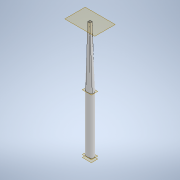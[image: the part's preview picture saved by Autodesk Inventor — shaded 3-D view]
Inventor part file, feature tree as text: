
AUTODESK INVENTOR PART (.ipt)
format: ipt  version: 2021 (Build 250183000, 183)  size: 248,320 bytes
history: native  units: mm
features: sketch x7, loft x6, other x4, plane x3
ambient origin geometry x8: Origin, YZ Plane, XZ Plane, XY Plane, X Axis, Y Axis, Z Axis, Center Point
bodies: Body1 (feature_tree)
feature tree (20):
  sketch  "Sketch1"  dims[d0=463.0mm d8=22.0mm]
  plane  "Work Plane1"
  sketch  "Sketch2"  dims[d9=32.0mm d11=19.0mm]
  sketch  "Sketch3"  dims[d16=15.0mm d17=15.0mm]
  plane  "Work Plane3"
  sketch  "Sketch5"  dims[d19=20.0mm d20=30.0mm]
  sketch  "Sketch6"  dims[d25=-455.0mm d26=20.0mm d27=22.0mm]
  sketch  "Sketch7"  dims[d28=32.0mm d29=30.0mm]
  sketch  "Sketch8"  dims[d30=20.0mm d31=10.0mm d32=12.0mm d33=0.0mm d34=90.0deg d35=0.0mm d36=90.0deg d37=0.0mm d38=90.0deg d39=0.0mm d40=90.0deg d41=0.0mm d42=90.0deg d43=0.0mm d44=90.0deg d45=0.0mm d46=90.0deg d47=0.0mm d48=90.0deg d49=0.0mm d50=90.0deg d51=0.0mm d52=90.0deg d53=0.0mm d54=90.0deg d55=0.0mm d56=90.0deg d12=0.5mm d13=0.872665mm d14=0.5mm d15=0.872665mm]
  loft  "Loft3"
  loft  "Loft4"
  loft  "Loft5"
  loft  "Loft6"
  loft  "Loft7"
  loft  "Loft8"
  plane  "Work Plane2"
  other  "Edges1"
  other  "Edges2"
  other  "Edges3"
  other  "Edges4"
